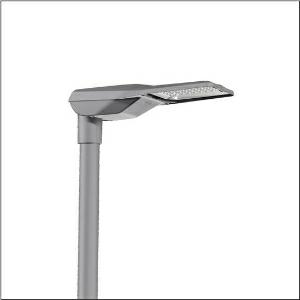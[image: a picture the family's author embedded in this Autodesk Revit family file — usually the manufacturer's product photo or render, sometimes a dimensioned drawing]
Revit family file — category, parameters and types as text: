
# Revit family: streetlight_sl_21_iq_mini___stw1_0a_5xe2e31g08gb_0d22
name_source: partatom
category: Lighting Fixtures
units: mm (PartAtom-declared; Revit-internal decimal feet)

## family parameters
Cut with Voids When Loaded = No
Host = Face
Light Source = No
Part Type = Normal
Room Calculation Point = No
Round Connector Dimension = Use Diameter
Shared = No

## types (1)
- --- (1 x LED, 5680 lm, 37.1 W, 3000K)
    Apparent Load = 37 VA
    CIE Flux Codes = 38 75 98 100 100
    Color Rendering = 70
    Color Temperature = 3000K
    Default Elevation = 1800 mm
    Description = Streetlight SL 21 iQ mini, mast luminaire, primary light control with lens, of PMMA, primary optical cover: cover, of toughened safety glass, transparent, light distribution: STW1.0a, light emission: direct distribution, primary light characteristic: asymmetric, installation type: post-top, side-entry, LED, High Power LED, rated luminous flux: 5.680lm, luminous efficacy: 153lm/W, light colour: 730, colour temperature: 3000K, control gear: iQ Street-Remote, control: Street-Remote, Auto-Match, Temp-Guard, Lumen-Switch, Night-Set, Smart-Wire, Light-Fading, Desk-Remote (wireless, voltage-free reading and setting of iQ features in the workshop via application-optimized NFC function/RFID function), optimised constant luminous flux control (CLO 2.0), pre-setting: linear dimming characteristic, mains connection: 220..240V, AC, 50/60Hz, start of lifetime: 37W, end of service life: 39W, reduction: 18W, luminaire housing, of diecast aluminium, powder-coated, Siteco® metallic grey (DB 702S), corrosivity category C5 mid according to DIN EN ISO 12944, please order mast flange separately, inclination adjustable: 0°, 5°, 10°, 15°, sealing non-destructively replaceable, multi-level sealing system, length: 628mm, width: 235mm, height: 110mm, mast flange for spigot size: 42mm (side-entry): 5XC10008XM4, 60/48mm (side-entry/post-top): 5XC10108XM2, 76/60mm (side-entry/post-top): 5XC10108XM1, mounting height: 4..8m, protection rating (complete): IP66, insulation class (complete): insulation class II (safety insulation), certification: CE, ENEC, ENEC+, VDE, impact resistance: IK10, permissible operating ambient temperature for outdoor applications: -40..+50°C, standard-compliant lighting for roads and squares, packaging unit: 1 piece

Light Distribution: STW1.0a
    Height = 110 mm
    Lamp = 1 x LED
    Lamp Light Flux = 5680 lm
    Lamp Power = 37.1 W
    Lamp count = 1
    Length = 625 mm
    Luminous efficacy = 153 lm/W
    Manufacturer = Siteco
    ModVariant = No
    Model = 5XE2E31G08GB
    Number of Poles = 1
    OnlyDefault = Yes
    Power Factor = 1
    Product Name = Streetlight SL 21 iQ mini | STW1.0a
    Product group = mast luminaire | pylon top
    ProductGroupID = 6100
    Protection Class = Protection class II
    Protection Degree = IP 66
    RLX_Detail_Level = 1
    RLX_Emergency_Light_Flux = 0 lm
    RLX_Emergency_Type = 0
    RLX_Emergency_Type_DB = No
    RlxData = <blob elided: 26421 chars, md5=283d5a61>
    Socket = socket
    Standby Power = 0 W
    System Light Flux = 5680 lm
    System Power = 37 W
    Type Comments = factory setting: luminous flux: 100 % | dim-lin: 254 | 385 mA
    Type Image = l_1003519.jpg
    URL = http://relux.com
    VarID = @adj_208859
    Voltage = 0 V
    Weight = 0.00 kg
    Width = 234 mm

## geometry (parser evidence)
native form markers: Blend x4, Sweep x9
no freeform markers — native parametric forms only
